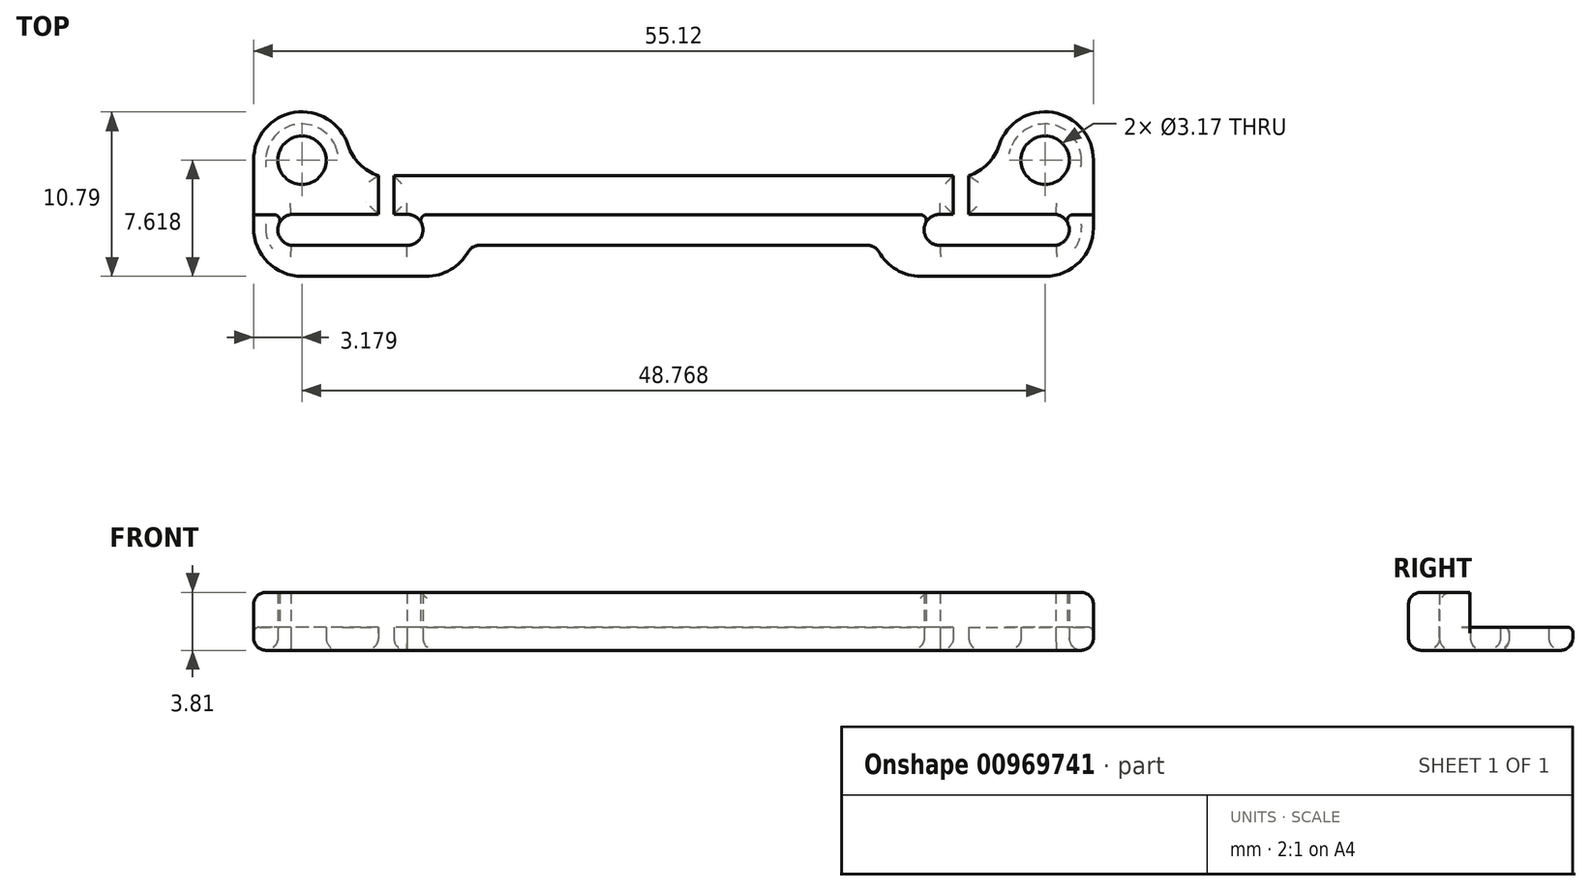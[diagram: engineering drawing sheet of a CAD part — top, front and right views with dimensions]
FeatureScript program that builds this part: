
annotation { "Feature Type Name" : "Feature", "Feature Type Description" : "" }
export const myFeature = defineFeature(function(context is Context, id is Id, definition is map)
    precondition{}
    {
        {
            var Q0;
            Q0=qCreatedBy(makeId("Top.planeOp"),FACE);
            var sketch = newSketch(context, id + "F0", { "sketchPlane" : qUnion([Q0])});
            skLineSegment(sketch, "E0", {"start": v(-29.34, -33.33) * mm, "end": v(-29.34, -17.07) * mm});
            skLineSegment(sketch, "E1", {"start": v(-32.75, -29.77) * mm, "end": v(29.96, -29.77) * mm, "construction": true});
            skLineSegment(sketch, "E2", {"start": v(-25.78, 34.73) * mm, "end": v(-25.78, -35.44) * mm, "construction": true});
            skLineSegment(sketch, "E3", {"start": v(22.99, 35.22) * mm, "end": v(22.99, -36.91) * mm, "construction": true});
            skCircle(sketch, "E4", {"center": v(-25.78, -29.77) * mm, "radius": 1.59 * mm});
            skCircle(sketch, "E5", {"center": v(22.99, -29.77) * mm, "radius": 1.59 * mm});
            skArc(sketch, "E6", {"start": v(-22.77, -30.79) * mm, "mid": v(-25.27, -26.64) * mm, "end": v(-28.96, -29.77) * mm});
            skArc(sketch, "E7", {"start": v(22.99, -32.95) * mm, "mid": v(24.84, -27.2) * mm, "end": v(19.98, -30.79) * mm});
            skLineSegment(sketch, "E8", {"start": v(-29.34, -33.33) * mm, "end": v(-29.34, -44.2) * mm});
            skLineSegment(sketch, "E9", {"start": v(-28.96, -37.4) * mm, "end": v(-14.67, -37.4) * mm});
            skLineSegment(sketch, "E10", {"start": v(-14.67, -35.36) * mm, "end": v(-14.67, -37.4) * mm});
            skLineSegment(sketch, "E11", {"start": v(-28.96, -29.77) * mm, "end": v(-28.96, -37.4) * mm});
            skLineSegment(sketch, "E12.trimOffspring", {"start": v(-18.84, -33.33) * mm, "end": v(-19.76, -33.33) * mm});
            skLineSegment(sketch, "E13.trimOffspring", {"start": v(-14.67, -35.36) * mm, "end": v(-1.4, -35.36) * mm});
            skPoint(sketch, "E14.orphan", {"position": v(-29.34, -37.4) * mm});
            skArc(sketch, "E15", {"start": v(-18.9, -35.36) * mm, "mid": v(-17.84, -34.35) * mm, "end": v(-18.88, -33.33) * mm});
            skArc(sketch, "E16", {"start": v(-26.5, -33.33) * mm, "mid": v(-27.37, -34.34) * mm, "end": v(-26.5, -35.36) * mm});
            skLineSegment(sketch, "E17", {"start": v(-19.76, -33.33) * mm, "end": v(-19.76, -30.79) * mm});
            skLineSegment(sketch, "E18", {"start": v(-20.77, -33.33) * mm, "end": v(-20.77, -30.79) * mm});
            skLineSegment(sketch, "E19.trimOffspring", {"start": v(-26.5, -35.36) * mm, "end": v(-18.82, -35.36) * mm});
            skLineSegment(sketch, "E20.trimOffspring", {"start": v(-27.37, -34.31) * mm, "end": v(-27.37, -34.37) * mm});
            skLineSegment(sketch, "E21.trimOffspring", {"start": v(-20.77, -33.33) * mm, "end": v(-26.5, -33.33) * mm});
            skLineSegment(sketch, "E22.trimOffspring", {"start": v(-19.76, -30.79) * mm, "end": v(-1.4, -30.79) * mm});
            skLineSegment(sketch, "E23.trimOffspring", {"start": v(-22.77, -30.79) * mm, "end": v(-20.77, -30.79) * mm});
            skLineSegment(sketch, "E24", {"start": v(-1.4, -30.79) * mm, "end": v(-1.4, -40.59) * mm});
            skLineSegment(sketch, "E25.MirrorCS", {"start": v(19.98, -30.79) * mm, "end": v(17.98, -30.79) * mm});
            skLineSegment(sketch, "E26.MirrorCS", {"start": v(17.98, -33.33) * mm, "end": v(17.98, -30.79) * mm});
            skLineSegment(sketch, "E27.MirrorCS", {"start": v(16.96, -33.33) * mm, "end": v(16.96, -30.79) * mm});
            skLineSegment(sketch, "E28.MirrorCS", {"start": v(16.96, -30.79) * mm, "end": v(-1.4, -30.79) * mm});
            skLineSegment(sketch, "E29.MirrorCS", {"start": v(16.04, -33.33) * mm, "end": v(16.96, -33.33) * mm});
            skArc(sketch, "E30.MirrorCS", {"start": v(16.1, -35.36) * mm, "mid": v(15.05, -34.35) * mm, "end": v(16.09, -33.33) * mm});
            skLineSegment(sketch, "E31.MirrorCS", {"start": v(23.7, -35.36) * mm, "end": v(16.03, -35.36) * mm});
            skArc(sketch, "E32.MirrorCS", {"start": v(23.7, -33.33) * mm, "mid": v(24.57, -34.34) * mm, "end": v(23.7, -35.36) * mm});
            skLineSegment(sketch, "E33.MirrorCS", {"start": v(17.98, -33.33) * mm, "end": v(23.7, -33.33) * mm});
            skLineSegment(sketch, "E34.MirrorCS", {"start": v(26.16, -29.77) * mm, "end": v(26.16, -37.4) * mm});
            skLineSegment(sketch, "E35.MirrorCS", {"start": v(26.16, -37.4) * mm, "end": v(11.87, -37.4) * mm});
            skLineSegment(sketch, "E36.MirrorCS", {"start": v(11.87, -35.36) * mm, "end": v(11.87, -37.4) * mm});
            skLineSegment(sketch, "E37.MirrorCS", {"start": v(11.87, -35.36) * mm, "end": v(-1.4, -35.36) * mm});
            skSolve(sketch);
        }
        {
            var Q0;
            Q0=makeQuery(id+"F0.imprint","IMPRINT",FACE,{"disambiguationData":[TD([[makeQuery(id+"F0.imprint","IMPRINT",EDGE,{"derivedFrom":sQuery(id+"F0.wireOp",EDGE,"E5")}),-1.0]])]});
            var Q1;
            Q1=makeQuery(id+"F0.imprint","IMPRINT",FACE,{"disambiguationData":[TD([[makeQuery(id+"F0.imprint","IMPRINT",EDGE,{"derivedFrom":sQuery(id+"F0.wireOp",EDGE,"E4")}),-1.0]])]});
            extrude(context, id + "F1", {"entities" : qUnion([Q0, Q1]), "depth" : 1.52 * mm, "offsetDistance" : 25.4 * mm});
        }
        {
            var Q0;
            Q0=makeQuery(id+"F1.opExtrude","CAP_FACE",FACE,{"disambiguationData":[OSD([sQuery(id+"F0.wireOp",EDGE,"E4"),sQuery(id+"F0.wireOp",EDGE,"E5"),sQuery(id+"F0.wireOp",EDGE,"E6"),sQuery(id+"F0.wireOp",EDGE,"E7"),sQuery(id+"F0.wireOp",EDGE,"E9"),sQuery(id+"F0.wireOp",EDGE,"E10"),sQuery(id+"F0.wireOp",EDGE,"E11"),sQuery(id+"F0.wireOp",EDGE,"E12.trimOffspring"),sQuery(id+"F0.wireOp",EDGE,"E13.trimOffspring"),sQuery(id+"F0.wireOp",EDGE,"E15"),sQuery(id+"F0.wireOp",EDGE,"E16"),sQuery(id+"F0.wireOp",EDGE,"E17"),sQuery(id+"F0.wireOp",EDGE,"E18"),sQuery(id+"F0.wireOp",EDGE,"E19.trimOffspring"),sQuery(id+"F0.wireOp",EDGE,"E21.trimOffspring"),sQuery(id+"F0.wireOp",EDGE,"E22.trimOffspring"),sQuery(id+"F0.wireOp",EDGE,"E23.trimOffspring"),sQuery(id+"F0.wireOp",EDGE,"E25.MirrorCS"),sQuery(id+"F0.wireOp",EDGE,"E26.MirrorCS"),sQuery(id+"F0.wireOp",EDGE,"E27.MirrorCS"),sQuery(id+"F0.wireOp",EDGE,"E28.MirrorCS"),sQuery(id+"F0.wireOp",EDGE,"E29.MirrorCS"),sQuery(id+"F0.wireOp",EDGE,"E30.MirrorCS"),sQuery(id+"F0.wireOp",EDGE,"E31.MirrorCS"),sQuery(id+"F0.wireOp",EDGE,"E32.MirrorCS"),sQuery(id+"F0.wireOp",EDGE,"E33.MirrorCS"),sQuery(id+"F0.wireOp",EDGE,"E34.MirrorCS"),sQuery(id+"F0.wireOp",EDGE,"E35.MirrorCS"),sQuery(id+"F0.wireOp",EDGE,"E36.MirrorCS"),sQuery(id+"F0.wireOp",EDGE,"E37.MirrorCS")])],"isStart":false});
            var sketch = newSketch(context, id + "F2", { "sketchPlane" : qUnion([Q0])});
            skLineSegment(sketch, "E38.bottom", {"start": v(-28.96, -37.4) * mm, "end": v(26.16, -37.4) * mm});
            skLineSegment(sketch, "E38.top", {"start": v(-28.96, -33.35) * mm, "end": v(26.16, -33.35) * mm});
            skLineSegment(sketch, "E38.left", {"start": v(-28.96, -37.4) * mm, "end": v(-28.96, -33.35) * mm});
            skLineSegment(sketch, "E38.right", {"start": v(26.16, -37.4) * mm, "end": v(26.16, -33.35) * mm});
            skSolve(sketch);
        }
        {
            var Q0;
            {var subQ2=sQuery(id+"F2.wireOp",EDGE,"E38.left");Q0=makeQuery(id+"F2.imprint","IMPRINT",FACE,{"disambiguationData":[TD([[makeQuery(id+"F2.imprint","IMPRINT",EDGE,{"derivedFrom":subQ2}),1.0]])]});}
            extrude(context, id + "F3", {"entities" : qUnion([Q0]), "operationType" : NewBodyOperationType.ADD, "depth" : 2.3 * mm, "offsetDistance" : 25.4 * mm});
        }
        {
            var Q0;
            Q0=makeQuery(id+"F1.opExtrude","SWEPT_EDGE",EDGE,{"disambiguationData":[OSD([sQuery(id+"F0.wireOp",EDGE,"E6"),sQuery(id+"F0.wireOp",EDGE,"E23.trimOffspring")])]});
            var Q1;
            Q1=makeQuery(id+"F1.opExtrude","SWEPT_EDGE",EDGE,{"disambiguationData":[OSD([sQuery(id+"F0.wireOp",EDGE,"E7"),sQuery(id+"F0.wireOp",EDGE,"E25.MirrorCS")])]});
            var Q2;
            Q2=makeQuery(id+"F3.boolean.opBoolean","MERGE",EDGE,{"derivedFrom":[makeQuery(id+"F1.opExtrude","SWEPT_EDGE",EDGE,{"disambiguationData":[OSD([sQuery(id+"F0.wireOp",EDGE,"E34.MirrorCS"),sQuery(id+"F0.wireOp",EDGE,"E35.MirrorCS")])]}),makeQuery(id+"F3.opExtrude","SWEPT_EDGE",EDGE,{"disambiguationData":[OSD([sQuery(id+"F2.wireOp",EDGE,"E38.bottom"),sQuery(id+"F2.wireOp",EDGE,"E38.right")])]})]});
            var Q3;
            {var subQ0=sQuery(id+"F0.wireOp",EDGE,"E36.MirrorCS");Q3=makeQuery(id+"F3.boolean.opBoolean","MERGE",EDGE,{"derivedFrom":[makeQuery(id+"F1.opExtrude","SWEPT_EDGE",EDGE,{"disambiguationData":[OSD([sQuery(id+"F0.wireOp",EDGE,"E35.MirrorCS"),subQ0])]}),makeQuery(id+"F3.opExtrude","SWEPT_EDGE",EDGE,{"disambiguationData":[OSD([subQ0,sQuery(id+"F2.wireOp",EDGE,"E38.bottom")])]})]});}
            var Q4;
            {var subQ0=sQuery(id+"F0.wireOp",EDGE,"E10");Q4=makeQuery(id+"F3.boolean.opBoolean","MERGE",EDGE,{"derivedFrom":[makeQuery(id+"F1.opExtrude","SWEPT_EDGE",EDGE,{"disambiguationData":[OSD([sQuery(id+"F0.wireOp",EDGE,"E9"),subQ0])]}),makeQuery(id+"F3.opExtrude","SWEPT_EDGE",EDGE,{"disambiguationData":[OSD([subQ0,sQuery(id+"F2.wireOp",EDGE,"E38.bottom")])]})]});}
            var Q5;
            Q5=makeQuery(id+"F3.boolean.opBoolean","MERGE",EDGE,{"derivedFrom":[makeQuery(id+"F1.opExtrude","SWEPT_EDGE",EDGE,{"disambiguationData":[OSD([sQuery(id+"F0.wireOp",EDGE,"E9"),sQuery(id+"F0.wireOp",EDGE,"E11")])]}),makeQuery(id+"F3.opExtrude","SWEPT_EDGE",EDGE,{"disambiguationData":[OSD([sQuery(id+"F2.wireOp",EDGE,"E38.bottom"),sQuery(id+"F2.wireOp",EDGE,"E38.left")])]})]});
            fillet(context, id + "F4", {"entities" : qUnion([Q0, Q1, Q2, Q3, Q4, Q5]), "radius" : 3.17 * mm, "tangentPropagation" : true, "allowEdgeOverflow" : false});
        }
        {
            var Q0;
            {var subQ0=sQuery(id+"F0.wireOp",EDGE,"E37.MirrorCS");var subQ1=sQuery(id+"F0.wireOp",EDGE,"E13.trimOffspring");var subQ2=sQuery(id+"F0.wireOp",EDGE,"E10");Q0=makeQuery(id+"F4.opFillet","BLEND_EDGE",EDGE,{"blendedFrom":[makeQuery(id+"F3.boolean.opBoolean","MERGE",EDGE,{"derivedFrom":[makeQuery(id+"F1.opExtrude","SWEPT_EDGE",EDGE,{"disambiguationData":[OSD([sQuery(id+"F0.wireOp",EDGE,"E9"),subQ2])]}),makeQuery(id+"F3.opExtrude","SWEPT_EDGE",EDGE,{"disambiguationData":[OSD([subQ2,sQuery(id+"F2.wireOp",EDGE,"E38.bottom")])]})]}),makeQuery(id+"F3.boolean.opBoolean","MERGE",FACE,{"derivedFrom":[makeQuery(id+"F1.opExtrude","SWEPT_FACE",FACE,{"disambiguationData":[OSD([subQ1,subQ0])]}),makeQuery(id+"F3.opExtrude","SWEPT_FACE",FACE,{"disambiguationData":[OSD([subQ1,subQ0])]})]})],"blendedInto":[makeQuery(id+"F3.boolean.opBoolean","MERGE",FACE,{"derivedFrom":[makeQuery(id+"F1.opExtrude","SWEPT_FACE",FACE,{"disambiguationData":[OSD([subQ1,subQ0])]}),makeQuery(id+"F3.opExtrude","SWEPT_FACE",FACE,{"disambiguationData":[OSD([subQ1,subQ0])]})]})]});}
            var Q1;
            {var subQ0=sQuery(id+"F0.wireOp",EDGE,"E37.MirrorCS");var subQ1=sQuery(id+"F0.wireOp",EDGE,"E13.trimOffspring");var subQ2=sQuery(id+"F0.wireOp",EDGE,"E36.MirrorCS");Q1=makeQuery(id+"F4.opFillet","BLEND_EDGE",EDGE,{"blendedFrom":[makeQuery(id+"F3.boolean.opBoolean","MERGE",EDGE,{"derivedFrom":[makeQuery(id+"F1.opExtrude","SWEPT_EDGE",EDGE,{"disambiguationData":[OSD([sQuery(id+"F0.wireOp",EDGE,"E35.MirrorCS"),subQ2])]}),makeQuery(id+"F3.opExtrude","SWEPT_EDGE",EDGE,{"disambiguationData":[OSD([subQ2,sQuery(id+"F2.wireOp",EDGE,"E38.bottom")])]})]}),makeQuery(id+"F3.boolean.opBoolean","MERGE",FACE,{"derivedFrom":[makeQuery(id+"F1.opExtrude","SWEPT_FACE",FACE,{"disambiguationData":[OSD([subQ1,subQ0])]}),makeQuery(id+"F3.opExtrude","SWEPT_FACE",FACE,{"disambiguationData":[OSD([subQ1,subQ0])]})]})],"blendedInto":[makeQuery(id+"F3.boolean.opBoolean","MERGE",FACE,{"derivedFrom":[makeQuery(id+"F1.opExtrude","SWEPT_FACE",FACE,{"disambiguationData":[OSD([subQ1,subQ0])]}),makeQuery(id+"F3.opExtrude","SWEPT_FACE",FACE,{"disambiguationData":[OSD([subQ1,subQ0])]})]})]});}
            var Q2;
            Q2=makeQuery(id+"F1.opExtrude","CAP_FACE",FACE,{"disambiguationData":[OSD([sQuery(id+"F0.wireOp",EDGE,"E4"),sQuery(id+"F0.wireOp",EDGE,"E5"),sQuery(id+"F0.wireOp",EDGE,"E6"),sQuery(id+"F0.wireOp",EDGE,"E7"),sQuery(id+"F0.wireOp",EDGE,"E9"),sQuery(id+"F0.wireOp",EDGE,"E10"),sQuery(id+"F0.wireOp",EDGE,"E11"),sQuery(id+"F0.wireOp",EDGE,"E12.trimOffspring"),sQuery(id+"F0.wireOp",EDGE,"E13.trimOffspring"),sQuery(id+"F0.wireOp",EDGE,"E15"),sQuery(id+"F0.wireOp",EDGE,"E16"),sQuery(id+"F0.wireOp",EDGE,"E17"),sQuery(id+"F0.wireOp",EDGE,"E18"),sQuery(id+"F0.wireOp",EDGE,"E19.trimOffspring"),sQuery(id+"F0.wireOp",EDGE,"E21.trimOffspring"),sQuery(id+"F0.wireOp",EDGE,"E22.trimOffspring"),sQuery(id+"F0.wireOp",EDGE,"E23.trimOffspring"),sQuery(id+"F0.wireOp",EDGE,"E25.MirrorCS"),sQuery(id+"F0.wireOp",EDGE,"E26.MirrorCS"),sQuery(id+"F0.wireOp",EDGE,"E27.MirrorCS"),sQuery(id+"F0.wireOp",EDGE,"E28.MirrorCS"),sQuery(id+"F0.wireOp",EDGE,"E29.MirrorCS"),sQuery(id+"F0.wireOp",EDGE,"E30.MirrorCS"),sQuery(id+"F0.wireOp",EDGE,"E31.MirrorCS"),sQuery(id+"F0.wireOp",EDGE,"E32.MirrorCS"),sQuery(id+"F0.wireOp",EDGE,"E33.MirrorCS"),sQuery(id+"F0.wireOp",EDGE,"E34.MirrorCS"),sQuery(id+"F0.wireOp",EDGE,"E35.MirrorCS"),sQuery(id+"F0.wireOp",EDGE,"E36.MirrorCS"),sQuery(id+"F0.wireOp",EDGE,"E37.MirrorCS")])],"isStart":true});
            fillet(context, id + "F5", {"entities" : qUnion([Q0, Q1, Q2]), "radius" : 0.81 * mm, "tangentPropagation" : true, "allowEdgeOverflow" : false});
        }
        {
            var Q0;
            Q0=makeQuery(id+"F3.opExtrude","CAP_EDGE",EDGE,{"disambiguationData":[OSD([sQuery(id+"F2.wireOp",EDGE,"E38.right")])],"isStart":false});
            fillet(context, id + "F6", {"entities" : qUnion([Q0]), "radius" : 0.81 * mm, "tangentPropagation" : true, "allowEdgeOverflow" : false});
        }
        {
            var Q0;
            Q0=makeQuery(id+"F1.opExtrude","CAP_EDGE",EDGE,{"disambiguationData":[OSD([sQuery(id+"F0.wireOp",EDGE,"E34.MirrorCS")])],"isStart":false});
            var Q1;
            Q1=makeQuery(id+"F1.opExtrude","CAP_EDGE",EDGE,{"disambiguationData":[OSD([sQuery(id+"F0.wireOp",EDGE,"E22.trimOffspring"),sQuery(id+"F0.wireOp",EDGE,"E28.MirrorCS")])],"isStart":false});
            var Q2;
            {var subQ0=sQuery(id+"F0.wireOp",EDGE,"E16");var subQ1=sQuery(id+"F0.wireOp",EDGE,"E11");var subQ3=sQuery(id+"F0.wireOp",EDGE,"E6");var subQ4=sQuery(id+"F0.wireOp",EDGE,"E4");var subQ5=sQuery(id+"F0.wireOp",EDGE,"E18");var subQ6=sQuery(id+"F0.wireOp",EDGE,"E21.trimOffspring");var subQ8=sQuery(id+"F0.wireOp",EDGE,"E23.trimOffspring");Q2=makeQuery(id+"F4.opFillet","BLEND_EDGE",EDGE,{"blendedFrom":[makeQuery(id+"F1.opExtrude","SWEPT_EDGE",EDGE,{"disambiguationData":[OSD([subQ3,subQ8])]}),makeQuery(id+"F3.boolean.opBoolean","SPLIT",FACE,{"disambiguationData":[TD([makeQuery(id+"F1.opExtrude","SWEPT_FACE",FACE,{"disambiguationData":[OSD([subQ4])]})])],"derivedFrom":makeQuery(id+"F1.opExtrude","CAP_FACE",FACE,{"disambiguationData":[OSD([subQ4,sQuery(id+"F0.wireOp",EDGE,"E5"),subQ3,sQuery(id+"F0.wireOp",EDGE,"E7"),sQuery(id+"F0.wireOp",EDGE,"E9"),sQuery(id+"F0.wireOp",EDGE,"E10"),subQ1,sQuery(id+"F0.wireOp",EDGE,"E12.trimOffspring"),sQuery(id+"F0.wireOp",EDGE,"E13.trimOffspring"),sQuery(id+"F0.wireOp",EDGE,"E15"),subQ0,sQuery(id+"F0.wireOp",EDGE,"E17"),subQ5,sQuery(id+"F0.wireOp",EDGE,"E19.trimOffspring"),subQ6,sQuery(id+"F0.wireOp",EDGE,"E22.trimOffspring"),subQ8,sQuery(id+"F0.wireOp",EDGE,"E25.MirrorCS"),sQuery(id+"F0.wireOp",EDGE,"E26.MirrorCS"),sQuery(id+"F0.wireOp",EDGE,"E27.MirrorCS"),sQuery(id+"F0.wireOp",EDGE,"E28.MirrorCS"),sQuery(id+"F0.wireOp",EDGE,"E29.MirrorCS"),sQuery(id+"F0.wireOp",EDGE,"E30.MirrorCS"),sQuery(id+"F0.wireOp",EDGE,"E31.MirrorCS"),sQuery(id+"F0.wireOp",EDGE,"E32.MirrorCS"),sQuery(id+"F0.wireOp",EDGE,"E33.MirrorCS"),sQuery(id+"F0.wireOp",EDGE,"E34.MirrorCS"),sQuery(id+"F0.wireOp",EDGE,"E35.MirrorCS"),sQuery(id+"F0.wireOp",EDGE,"E36.MirrorCS"),sQuery(id+"F0.wireOp",EDGE,"E37.MirrorCS")])],"isStart":false})})],"blendedInto":[makeQuery(id+"F3.boolean.opBoolean","SPLIT",FACE,{"disambiguationData":[TD([makeQuery(id+"F1.opExtrude","SWEPT_FACE",FACE,{"disambiguationData":[OSD([subQ4])]})])],"derivedFrom":makeQuery(id+"F1.opExtrude","CAP_FACE",FACE,{"disambiguationData":[OSD([subQ4,sQuery(id+"F0.wireOp",EDGE,"E5"),subQ3,sQuery(id+"F0.wireOp",EDGE,"E7"),sQuery(id+"F0.wireOp",EDGE,"E9"),sQuery(id+"F0.wireOp",EDGE,"E10"),subQ1,sQuery(id+"F0.wireOp",EDGE,"E12.trimOffspring"),sQuery(id+"F0.wireOp",EDGE,"E13.trimOffspring"),sQuery(id+"F0.wireOp",EDGE,"E15"),subQ0,sQuery(id+"F0.wireOp",EDGE,"E17"),subQ5,sQuery(id+"F0.wireOp",EDGE,"E19.trimOffspring"),subQ6,sQuery(id+"F0.wireOp",EDGE,"E22.trimOffspring"),subQ8,sQuery(id+"F0.wireOp",EDGE,"E25.MirrorCS"),sQuery(id+"F0.wireOp",EDGE,"E26.MirrorCS"),sQuery(id+"F0.wireOp",EDGE,"E27.MirrorCS"),sQuery(id+"F0.wireOp",EDGE,"E28.MirrorCS"),sQuery(id+"F0.wireOp",EDGE,"E29.MirrorCS"),sQuery(id+"F0.wireOp",EDGE,"E30.MirrorCS"),sQuery(id+"F0.wireOp",EDGE,"E31.MirrorCS"),sQuery(id+"F0.wireOp",EDGE,"E32.MirrorCS"),sQuery(id+"F0.wireOp",EDGE,"E33.MirrorCS"),sQuery(id+"F0.wireOp",EDGE,"E34.MirrorCS"),sQuery(id+"F0.wireOp",EDGE,"E35.MirrorCS"),sQuery(id+"F0.wireOp",EDGE,"E36.MirrorCS"),sQuery(id+"F0.wireOp",EDGE,"E37.MirrorCS")])],"isStart":false})})]});}
            var Q3;
            Q3=makeQuery(id+"F3.opExtrude","SWEPT_EDGE",EDGE,{"disambiguationData":[OSD([sQuery(id+"F0.wireOp",EDGE,"E32.MirrorCS"),sQuery(id+"F2.wireOp",EDGE,"E38.top")])]});
            var Q4;
            Q4=makeQuery(id+"F3.opExtrude","SWEPT_EDGE",EDGE,{"disambiguationData":[OSD([sQuery(id+"F0.wireOp",EDGE,"E16"),sQuery(id+"F2.wireOp",EDGE,"E38.top")])]});
            var Q5;
            Q5=makeQuery(id+"F3.opExtrude","SWEPT_EDGE",EDGE,{"disambiguationData":[OSD([sQuery(id+"F0.wireOp",EDGE,"E30.MirrorCS"),sQuery(id+"F2.wireOp",EDGE,"E38.top")])]});
            var Q6;
            Q6=makeQuery(id+"F3.opExtrude","SWEPT_EDGE",EDGE,{"disambiguationData":[OSD([sQuery(id+"F0.wireOp",EDGE,"E15"),sQuery(id+"F2.wireOp",EDGE,"E38.top")])]});
            var Q7;
            {var subQ0=sQuery(id+"F2.wireOp",EDGE,"E38.top");Q7=makeQuery(id+"F3.opExtrude","CAP_EDGE",EDGE,{"disambiguationData":[OSD([subQ0]),TDD([makeQuery(id+"F2.imprint","IMPRINT",EDGE,{"disambiguationData":[TD([[makeQuery(id+"F2.imprint","INTERSECT",VERTEX,{"derivedFrom":[makeQuery(id+"F1.opExtrude","CAP_EDGE",EDGE,{"disambiguationData":[OSD([sQuery(id+"F0.wireOp",EDGE,"E15")])],"isStart":false}),subQ0]}),-1.0]])],"derivedFrom":subQ0})])],"isStart":false});}
            var Q8;
            {var subQ0=sQuery(id+"F2.wireOp",EDGE,"E38.top");Q8=makeQuery(id+"F3.opExtrude","CAP_EDGE",EDGE,{"disambiguationData":[OSD([subQ0]),TDD([makeQuery(id+"F2.imprint","IMPRINT",EDGE,{"disambiguationData":[TD([[makeQuery(id+"F2.imprint","INTERSECT",VERTEX,{"derivedFrom":[makeQuery(id+"F1.opExtrude","CAP_EDGE",EDGE,{"disambiguationData":[OSD([sQuery(id+"F0.wireOp",EDGE,"E15")])],"isStart":false}),subQ0]}),-1.0]])],"derivedFrom":subQ0})])],"isStart":true});}
            fillet(context, id + "F7", {"entities" : qUnion([Q0, Q1, Q2, Q3, Q4, Q5, Q6, Q7, Q8]), "radius" : 0.38 * mm, "tangentPropagation" : true, "allowEdgeOverflow" : false});
        }
    });
